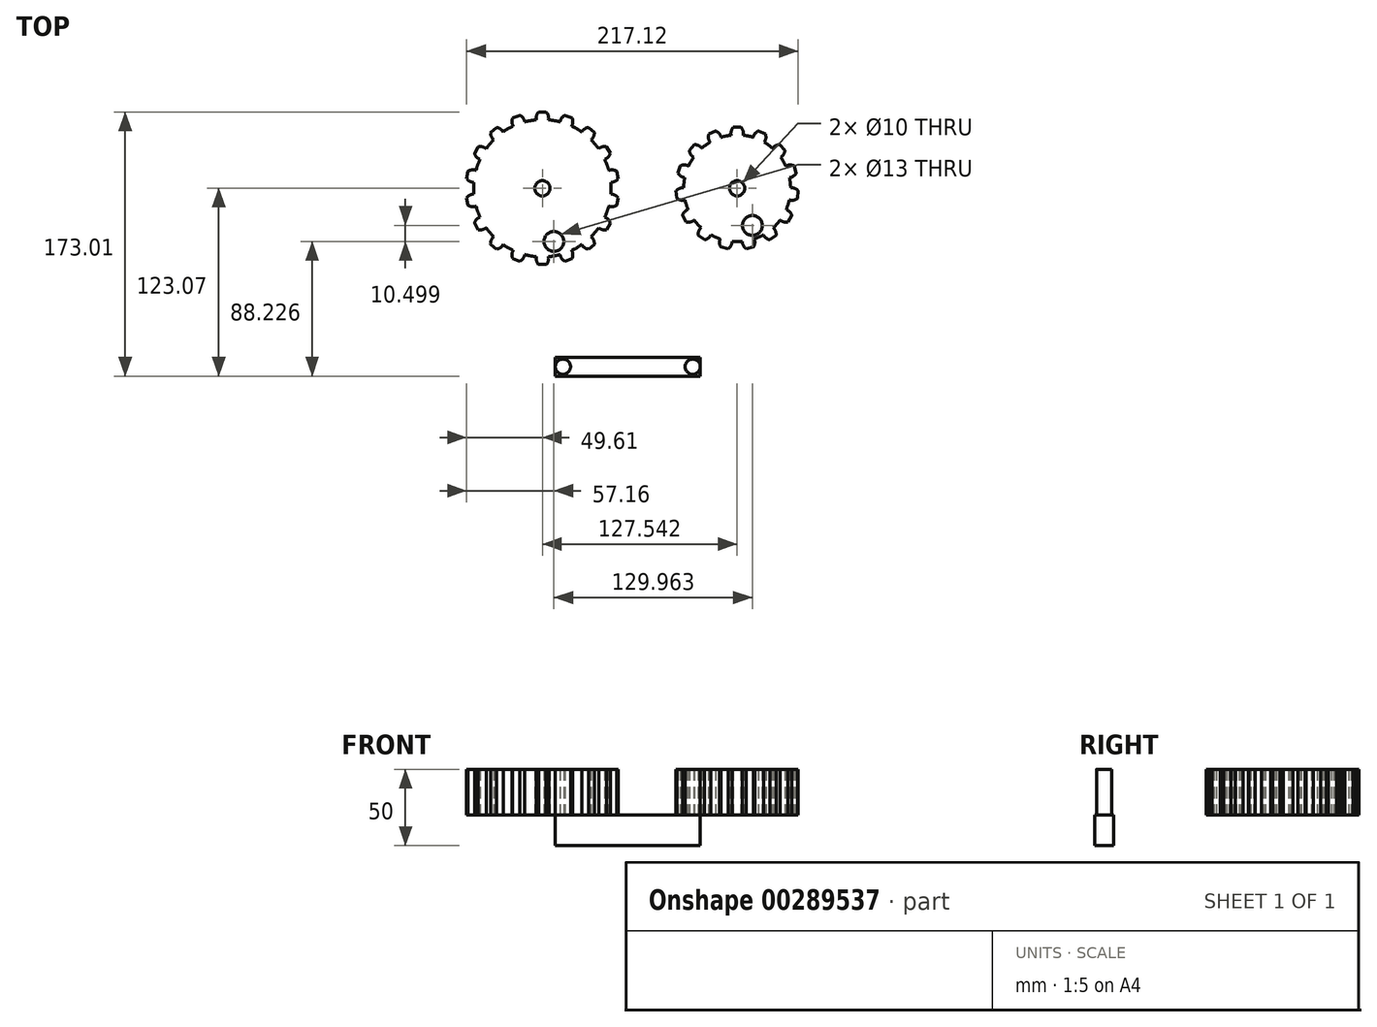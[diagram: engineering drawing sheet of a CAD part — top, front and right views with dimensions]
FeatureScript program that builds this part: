
annotation { "Feature Type Name" : "Feature", "Feature Type Description" : "" }
export const myFeature = defineFeature(function(context is Context, id is Id, definition is map)
    precondition{}
    {
        {
            var Q0;
            Q0=qCreatedBy(makeId("Top.planeOp"),FACE);
            var sketch = newSketch(context, id + "F0", { "sketchPlane" : qUnion([Q0])});
            skCircle(sketch, "E0", {"center": v(0, 0) * mm, "radius": 50 * mm, "construction": true});
            skArc(sketch, "E1", {"start": v(-4, 44.82) * mm, "mid": v(0, -45) * mm, "end": v(4, 44.82) * mm});
            skLineSegment(sketch, "E2", {"start": v(0, 50) * mm, "end": v(0, -50) * mm, "construction": true});
            skLineSegment(sketch, "E3", {"start": v(-2.5, 49.94) * mm, "end": v(2.5, 49.94) * mm});
            skLineSegment(sketch, "E4", {"start": v(-4, 44.82) * mm, "end": v(4, 44.82) * mm});
            skArc(sketch, "E5", {"start": v(4, 44.82) * mm, "mid": v(3.85, 47.56) * mm, "end": v(2.5, 49.94) * mm});
            skArc(sketch, "E6", {"start": v(-2.5, 49.94) * mm, "mid": v(-3.85, 47.56) * mm, "end": v(-4, 44.82) * mm});
            skCircle(sketch, "E7", {"center": v(0, 0) * mm, "radius": 5 * mm});
            skCircle(sketch, "E8", {"center": v(7.55, -34.84) * mm, "radius": 6.5 * mm});
            skSolve(sketch);
        }
        {
            var Q0;
            Q0=makeQuery(id+"F0.imprint","IMPRINT",FACE,{"disambiguationData":[TD([[makeQuery(id+"F0.imprint","IMPRINT",EDGE,{"derivedFrom":sQuery(id+"F0.wireOp",EDGE,"E3")}),-1.0]])]});
            extrude(context, id + "F1", {"entities" : qUnion([Q0]), "depth" : 30 * mm});
        }
        {
            var Q0;
            Q0=makeQuery(id+"F0.imprint","IMPRINT",FACE,{"disambiguationData":[TD([[makeQuery(id+"F0.imprint","IMPRINT",EDGE,{"derivedFrom":sQuery(id+"F0.wireOp",EDGE,"E1")}),1.0]])]});
            extrude(context, id + "F2", {"entities" : qUnion([Q0]), "depth" : 30 * mm});
        }
        {
            var Q0;
            Q0=makeQuery(id+"F1.opExtrude","SWEPT_BODY",BODY,{"disambiguationData":[OSD([sQuery(id+"F0.wireOp",EDGE,"E3"),sQuery(id+"F0.wireOp",EDGE,"E4"),sQuery(id+"F0.wireOp",EDGE,"E5"),sQuery(id+"F0.wireOp",EDGE,"E6")])]});
            var Q1;
            Q1=makeQuery(id+"F2.opExtrude","SWEPT_FACE",FACE,{"disambiguationData":[OSD([sQuery(id+"F0.wireOp",EDGE,"E1")])]});
            circularPattern(context, id + "F3", {"operationType" : NewBodyOperationType.ADD, "entities" : qUnion([Q0]), "axis" : qUnion([Q1]), "angle" : 360 * degree, "instanceCount" : 18, "oppositeDirection" : true, "equalSpace" : true});
        }
        {
            var Q0;
            Q0=qCreatedBy(makeId("Top.planeOp"),FACE);
            var sketch = newSketch(context, id + "F4", { "sketchPlane" : qUnion([Q0])});
            skCircle(sketch, "E9", {"center": v(127.54, 0) * mm, "radius": 40 * mm, "construction": true});
            skArc(sketch, "E10", {"start": v(123.54, 34.77) * mm, "mid": v(127.54, -35) * mm, "end": v(131.54, 34.77) * mm});
            skLineSegment(sketch, "E11", {"start": v(127.54, 40) * mm, "end": v(127.54, -40) * mm, "construction": true});
            skLineSegment(sketch, "E12", {"start": v(125.04, 39.92) * mm, "end": v(130.04, 39.92) * mm});
            skLineSegment(sketch, "E13", {"start": v(123.54, 34.77) * mm, "end": v(131.54, 34.77) * mm});
            skArc(sketch, "E14", {"start": v(125.04, 39.92) * mm, "mid": v(123.68, 37.52) * mm, "end": v(123.54, 34.77) * mm});
            skArc(sketch, "E15", {"start": v(131.54, 34.77) * mm, "mid": v(131.4, 37.52) * mm, "end": v(130.04, 39.92) * mm});
            skCircle(sketch, "E16", {"center": v(127.54, 0) * mm, "radius": 5 * mm});
            skCircle(sketch, "E17", {"center": v(137.51, -24.34) * mm, "radius": 6.5 * mm});
            skSolve(sketch);
        }
        {
            var Q0;
            Q0=makeQuery(id+"F4.imprint","IMPRINT",FACE,{"disambiguationData":[TD([[makeQuery(id+"F4.imprint","IMPRINT",EDGE,{"derivedFrom":sQuery(id+"F4.wireOp",EDGE,"E10")}),1.0]])]});
            extrude(context, id + "F5", {"entities" : qUnion([Q0]), "depth" : 30 * mm});
        }
        {
            var Q0;
            Q0=makeQuery(id+"F4.imprint","IMPRINT",FACE,{"disambiguationData":[TD([[makeQuery(id+"F4.imprint","IMPRINT",EDGE,{"derivedFrom":sQuery(id+"F4.wireOp",EDGE,"E12")}),-1.0]])]});
            extrude(context, id + "F6", {"entities" : qUnion([Q0]), "depth" : 30 * mm});
        }
        {
            var Q0;
            Q0=makeQuery(id+"F6.opExtrude","SWEPT_BODY",BODY,{"disambiguationData":[OSD([sQuery(id+"F4.wireOp",EDGE,"E12"),sQuery(id+"F4.wireOp",EDGE,"E13"),sQuery(id+"F4.wireOp",EDGE,"E14"),sQuery(id+"F4.wireOp",EDGE,"E15")])]});
            var Q1;
            Q1=makeQuery(id+"F5.opExtrude","SWEPT_FACE",FACE,{"disambiguationData":[OSD([sQuery(id+"F4.wireOp",EDGE,"E10")])]});
            circularPattern(context, id + "F7", {"operationType" : NewBodyOperationType.ADD, "entities" : qUnion([Q0]), "axis" : qUnion([Q1]), "angle" : 360 * degree, "instanceCount" : 15, "oppositeDirection" : true, "equalSpace" : true});
        }
        {
            var Q0;
            Q0=qCreatedBy(makeId("Top.planeOp"),FACE);
            var sketch = newSketch(context, id + "F8", { "sketchPlane" : qUnion([Q0])});
            skLineSegment(sketch, "E18.bottom", {"start": v(8.43, -110.7) * mm, "end": v(103.43, -110.7) * mm});
            skLineSegment(sketch, "E18.top", {"start": v(8.43, -123.07) * mm, "end": v(103.43, -123.07) * mm});
            skLineSegment(sketch, "E18.left", {"start": v(8.43, -110.7) * mm, "end": v(8.43, -123.07) * mm});
            skLineSegment(sketch, "E18.right", {"start": v(103.43, -110.7) * mm, "end": v(103.43, -123.07) * mm});
            skCircle(sketch, "E19", {"center": v(13.43, -116.88) * mm, "radius": 5 * mm});
            skCircle(sketch, "E20", {"center": v(98.43, -116.87) * mm, "radius": 5 * mm});
            skSolve(sketch);
        }
        {
            var Q0;
            Q0=makeQuery(id+"F8.imprint","IMPRINT",FACE,{"disambiguationData":[TD([[makeQuery(id+"F8.imprint","IMPRINT",EDGE,{"derivedFrom":sQuery(id+"F8.wireOp",EDGE,"E18.bottom")}),-1.0]])]});
            var Q1;
            Q1=makeQuery(id+"F8.imprint","IMPRINT",FACE,{"disambiguationData":[TD([[makeQuery(id+"F8.imprint","IMPRINT",EDGE,{"derivedFrom":sQuery(id+"F8.wireOp",EDGE,"E19")}),1.0]])]});
            var Q2;
            Q2=makeQuery(id+"F8.imprint","IMPRINT",FACE,{"disambiguationData":[TD([[makeQuery(id+"F8.imprint","IMPRINT",EDGE,{"derivedFrom":sQuery(id+"F8.wireOp",EDGE,"E20")}),1.0]])]});
            extrude(context, id + "F9", {"entities" : qUnion([Q0, Q1, Q2]), "oppositeDirection" : true, "depth" : 20 * mm});
        }
        {
            var Q0;
            Q0=makeQuery(id+"F8.imprint","IMPRINT",FACE,{"disambiguationData":[TD([[makeQuery(id+"F8.imprint","IMPRINT",EDGE,{"derivedFrom":sQuery(id+"F8.wireOp",EDGE,"E20")}),1.0]])]});
            var Q1;
            Q1=makeQuery(id+"F8.imprint","IMPRINT",FACE,{"disambiguationData":[TD([[makeQuery(id+"F8.imprint","IMPRINT",EDGE,{"derivedFrom":sQuery(id+"F8.wireOp",EDGE,"E19")}),1.0]])]});
            extrude(context, id + "F10", {"entities" : qUnion([Q0, Q1]), "operationType" : NewBodyOperationType.ADD, "depth" : 30 * mm});
        }
    });
